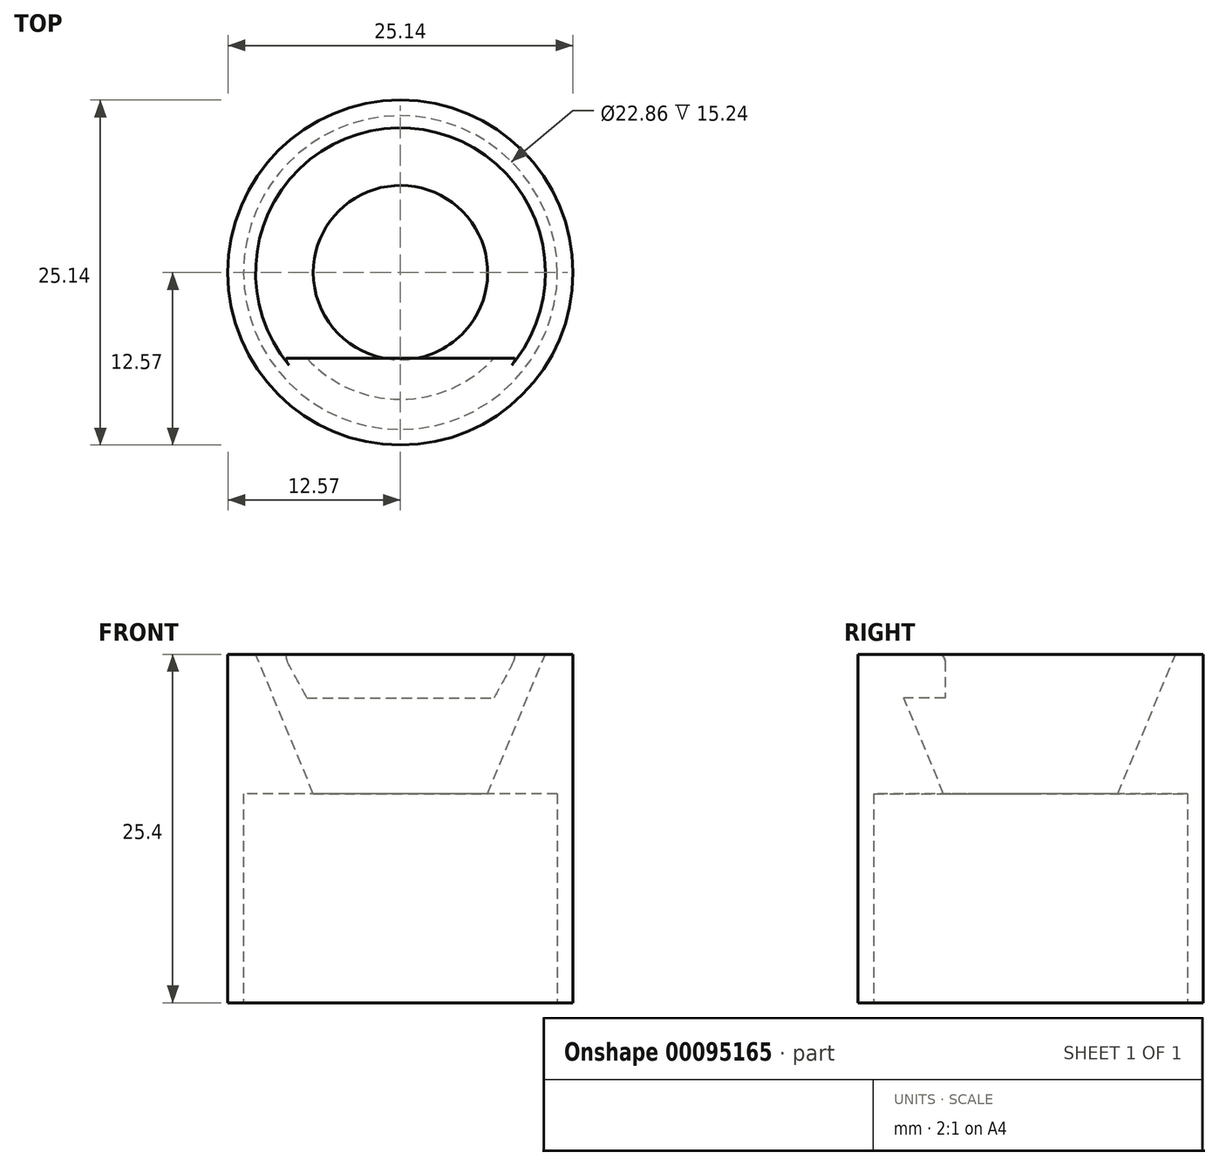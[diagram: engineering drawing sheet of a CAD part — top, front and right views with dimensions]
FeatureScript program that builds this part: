
annotation { "Feature Type Name" : "Feature", "Feature Type Description" : "" }
export const myFeature = defineFeature(function(context is Context, id is Id, definition is map)
    precondition{}
    {
        {
            var Q0;
            Q0=qCreatedBy(makeId("Top.planeOp"),FACE);
            var sketch = newSketch(context, id + "F0", { "sketchPlane" : qUnion([Q0])});
            skCircle(sketch, "E0", {"center": v(0, 0) * mm, "radius": 12.57 * mm});
            skSolve(sketch);
        }
        {
            var Q0;
            Q0 = qSketchRegion(id + "F0", true);
            extrude(context, id + "F1", {"entities" : qUnion([Q0]), "depth" : 25.4 * mm});
        }
        {
            var Q0;
            Q0=qCreatedBy(makeId("Top.planeOp"),FACE);
            var sketch = newSketch(context, id + "F2", { "sketchPlane" : qUnion([Q0])});
            skCircle(sketch, "E1", {"center": v(0, 0) * mm, "radius": 11.43 * mm});
            skSolve(sketch);
        }
        {
            var Q0;
            Q0 = qSketchRegion(id + "F2", true);
            extrude(context, id + "F3", {"entities" : qUnion([Q0]), "operationType" : NewBodyOperationType.REMOVE, "depth" : 15.24 * mm});
        }
        {
            var Q0;
            Q0=makeQuery(id+"F3.boolean.opBoolean","COPY",FACE,{"derivedFrom":makeQuery(id+"F3.opExtrude","CAP_FACE",FACE,{"disambiguationData":[OSD([sQuery(id+"F2.wireOp",EDGE,"E1")])],"isStart":false})});
            var sketch = newSketch(context, id + "F4", { "sketchPlane" : qUnion([Q0])});
            skCircle(sketch, "E2", {"center": v(0, 0) * mm, "radius": 6.35 * mm});
            skSolve(sketch);
        }
        {
            var Q0;
            Q0=makeQuery(id+"F1.opExtrude","CAP_FACE",FACE,{"disambiguationData":[OSD([sQuery(id+"F0.wireOp",EDGE,"E0")])],"isStart":false});
            var sketch = newSketch(context, id + "F5", { "sketchPlane" : qUnion([Q0])});
            skCircle(sketch, "E3", {"center": v(0, 0) * mm, "radius": 10.55 * mm});
            skSolve(sketch);
        }
        {
            var Q1;
            Q1=makeQuery(id+"F4.imprint","IMPRINT",FACE,{"disambiguationData":[TD([[makeQuery(id+"F4.imprint","IMPRINT",EDGE,{"derivedFrom":sQuery(id+"F4.wireOp",EDGE,"E2")}),1.0]])]});
            var Q2;
            Q2=makeQuery(id+"F5.imprint","IMPRINT",FACE,{"disambiguationData":[TD([[makeQuery(id+"F5.imprint","IMPRINT",EDGE,{"derivedFrom":sQuery(id+"F5.wireOp",EDGE,"E3")}),1.0]])]});
            loft(context, id + "F6", {"operationType" : NewBodyOperationType.REMOVE, "sheetProfilesArray" : [{ "sheetProfileEntities" : qUnion([Q1]) }, { "sheetProfileEntities" : qUnion([Q2]) }]});
        }
        {
            var Q0;
            Q0=makeQuery(id+"F1.opExtrude","CAP_FACE",FACE,{"disambiguationData":[OSD([sQuery(id+"F0.wireOp",EDGE,"E0")])],"isStart":false});
            var sketch = newSketch(context, id + "F7", { "sketchPlane" : qUnion([Q0])});
            skLineSegment(sketch, "E4", {"start": v(-10.92, -6.24) * mm, "end": v(10.92, -6.24) * mm});
            skArc(sketch, "E5", {"start": v(-10.92, -6.24) * mm, "mid": v(0, -12.04) * mm, "end": v(10.92, -6.24) * mm});
            skSolve(sketch);
        }
        {
            var Q0;
            Q0 = qSketchRegion(id + "F7", true);
            extrude(context, id + "F8", {"entities" : qUnion([Q0]), "operationType" : NewBodyOperationType.ADD, "oppositeDirection" : true, "depth" : 3.17 * mm});
        }
        {
            var Q0;
            Q0=makeQuery(id+"F6.boolean.opBoolean","COPY",EDGE,{"derivedFrom":makeQuery(id+"F6.opLoft","MID_CAP_EDGE",EDGE,{"disambiguationData":[OSD([sQuery(id+"F4.wireOp",EDGE,"E2"),sQuery(id+"F5.wireOp",EDGE,"E3")])],"capPos":1.0})});
            var Q1;
            Q1=makeQuery(id+"F8.opExtrude","CAP_EDGE",EDGE,{"disambiguationData":[OSD([sQuery(id+"F7.wireOp",EDGE,"E4")])],"isStart":true});
            fillet(context, id + "F9", {"entities" : qUnion([Q0, Q1]), "radius" : .5 * mm, "tangentPropagation" : true, "allowEdgeOverflow" : false});
        }
    });
